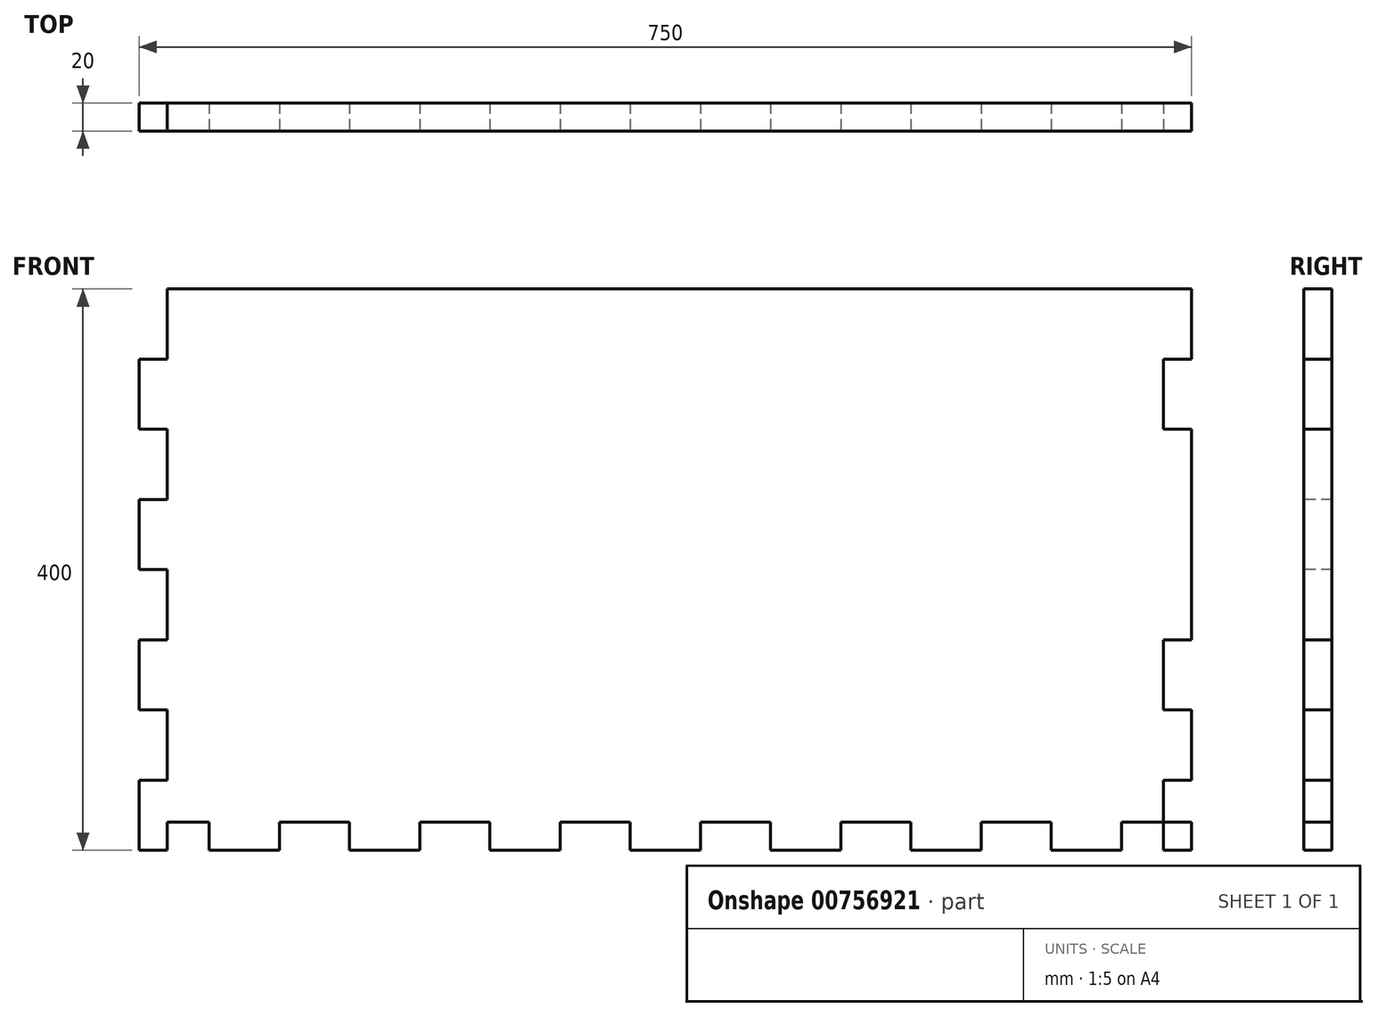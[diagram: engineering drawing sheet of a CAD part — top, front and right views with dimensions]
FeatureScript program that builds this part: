
annotation { "Feature Type Name" : "Feature", "Feature Type Description" : "" }
export const myFeature = defineFeature(function(context is Context, id is Id, definition is map)
    precondition{}
    {
        {
            var Q0;
            Q0=qCreatedBy(makeId("Front.planeOp"),FACE);
            var sketch = newSketch(context, id + "F0", { "sketchPlane" : qUnion([Q0])});
            skLineSegment(sketch, "E0.bottom", {"start": v(-370.9, 0) * mm, "end": v(379.1, 0) * mm});
            skLineSegment(sketch, "E0.top", {"start": v(-370.9, -400) * mm, "end": v(379.1, -400) * mm});
            skLineSegment(sketch, "E0.left", {"start": v(-370.9, 0) * mm, "end": v(-370.9, -400) * mm});
            skLineSegment(sketch, "E0.right", {"start": v(379.1, 0) * mm, "end": v(379.1, -400) * mm});
            skSolve(sketch);
        }
        {
            var Q0;
            Q0=makeQuery(id+"F0.imprint","IMPRINT",FACE,{"disambiguationData":[TD([[makeQuery(id+"F0.imprint","IMPRINT",EDGE,{"derivedFrom":sQuery(id+"F0.wireOp",EDGE,"E0.bottom")}),-1.0]])]});
            extrude(context, id + "F1", {"entities" : qUnion([Q0]), "depth" : 20 * mm, "offsetDistance" : 25.4 * mm});
        }
        {
            var Q0;
            Q0=makeQuery(id+"F1.opExtrude","CAP_FACE",FACE,{"disambiguationData":[OSD([sQuery(id+"F0.wireOp",EDGE,"E0.bottom"),sQuery(id+"F0.wireOp",EDGE,"E0.top"),sQuery(id+"F0.wireOp",EDGE,"E0.left"),sQuery(id+"F0.wireOp",EDGE,"E0.right")])],"isStart":false});
            var sketch = newSketch(context, id + "F2", { "sketchPlane" : qUnion([Q0])});
            skLineSegment(sketch, "E1.bottom", {"start": v(-370.9, 0) * mm, "end": v(-350.9, 0) * mm});
            skLineSegment(sketch, "E1.top", {"start": v(-370.9, -50) * mm, "end": v(-350.9, -50) * mm});
            skLineSegment(sketch, "E1.left", {"start": v(-370.9, 0) * mm, "end": v(-370.9, -50) * mm});
            skLineSegment(sketch, "E1.right", {"start": v(-350.9, 0) * mm, "end": v(-350.9, -50) * mm});
            skLineSegment(sketch, "E2.top", {"start": v(-370.9, -100) * mm, "end": v(-350.9, -100) * mm});
            skLineSegment(sketch, "E2.left", {"start": v(-370.9, -50) * mm, "end": v(-370.9, -100) * mm});
            skLineSegment(sketch, "E2.right", {"start": v(-350.9, -50) * mm, "end": v(-350.9, -100) * mm});
            skLineSegment(sketch, "E3.top", {"start": v(-370.9, -150) * mm, "end": v(-350.9, -150) * mm});
            skLineSegment(sketch, "E3.left", {"start": v(-370.9, -100) * mm, "end": v(-370.9, -150) * mm});
            skLineSegment(sketch, "E3.right", {"start": v(-350.9, -100) * mm, "end": v(-350.9, -150) * mm});
            skLineSegment(sketch, "E4.top", {"start": v(-370.9, -200) * mm, "end": v(-350.9, -200) * mm});
            skLineSegment(sketch, "E4.left", {"start": v(-370.9, -150) * mm, "end": v(-370.9, -200) * mm});
            skLineSegment(sketch, "E4.right", {"start": v(-350.9, -150) * mm, "end": v(-350.9, -200) * mm});
            skLineSegment(sketch, "E5.top", {"start": v(-370.9, -250) * mm, "end": v(-350.9, -250) * mm});
            skLineSegment(sketch, "E5.left", {"start": v(-370.9, -200) * mm, "end": v(-370.9, -250) * mm});
            skLineSegment(sketch, "E5.right", {"start": v(-350.9, -200) * mm, "end": v(-350.9, -250) * mm});
            skLineSegment(sketch, "E6.top", {"start": v(-370.9, -300) * mm, "end": v(-350.9, -300) * mm});
            skLineSegment(sketch, "E6.left", {"start": v(-370.9, -250) * mm, "end": v(-370.9, -300) * mm});
            skLineSegment(sketch, "E6.right", {"start": v(-350.9, -250) * mm, "end": v(-350.9, -300) * mm});
            skLineSegment(sketch, "E7.top", {"start": v(-370.9, -350) * mm, "end": v(-350.9, -350) * mm});
            skLineSegment(sketch, "E7.left", {"start": v(-370.9, -300) * mm, "end": v(-370.9, -350) * mm});
            skLineSegment(sketch, "E7.right", {"start": v(-350.9, -300) * mm, "end": v(-350.9, -350) * mm});
            skLineSegment(sketch, "E8.top", {"start": v(-370.9, -400) * mm, "end": v(-350.9, -400) * mm});
            skLineSegment(sketch, "E8.left", {"start": v(-370.9, -350) * mm, "end": v(-370.9, -400) * mm});
            skLineSegment(sketch, "E8.right", {"start": v(-350.9, -350) * mm, "end": v(-350.9, -400) * mm});
            skLineSegment(sketch, "E9.bottom", {"start": v(379.1, 0) * mm, "end": v(359.1, 0) * mm});
            skLineSegment(sketch, "E9.top", {"start": v(379.1, -50) * mm, "end": v(359.1, -50) * mm});
            skLineSegment(sketch, "E9.left", {"start": v(379.1, 0) * mm, "end": v(379.1, -50) * mm});
            skLineSegment(sketch, "E9.right", {"start": v(359.1, 0) * mm, "end": v(359.1, -50) * mm});
            skLineSegment(sketch, "E10.top", {"start": v(379.1, -100) * mm, "end": v(359.1, -100) * mm});
            skLineSegment(sketch, "E10.left", {"start": v(379.1, -50) * mm, "end": v(379.1, -100) * mm});
            skLineSegment(sketch, "E10.right", {"start": v(359.1, -50) * mm, "end": v(359.1, -100) * mm});
            skLineSegment(sketch, "E11.top", {"start": v(379.1, -150) * mm, "end": v(359.1, -150) * mm});
            skLineSegment(sketch, "E11.left", {"start": v(379.1, -100) * mm, "end": v(379.1, -150) * mm});
            skLineSegment(sketch, "E11.right", {"start": v(359.1, -100) * mm, "end": v(359.1, -150) * mm});
            skLineSegment(sketch, "E12.bottom", {"start": v(359.1, -150) * mm, "end": v(379.1, -150) * mm});
            skLineSegment(sketch, "E12.top", {"start": v(359.1, -200) * mm, "end": v(379.1, -200) * mm});
            skLineSegment(sketch, "E12.left", {"start": v(359.1, -150) * mm, "end": v(359.1, -200) * mm});
            skLineSegment(sketch, "E12.right", {"start": v(379.1, -150) * mm, "end": v(379.1, -200) * mm});
            skLineSegment(sketch, "E13.top", {"start": v(359.1, -250) * mm, "end": v(379.1, -250) * mm});
            skLineSegment(sketch, "E13.left", {"start": v(359.1, -200) * mm, "end": v(359.1, -250) * mm});
            skLineSegment(sketch, "E13.right", {"start": v(379.1, -200) * mm, "end": v(379.1, -250) * mm});
            skLineSegment(sketch, "E14.top", {"start": v(359.1, -300) * mm, "end": v(379.1, -300) * mm});
            skLineSegment(sketch, "E14.left", {"start": v(359.1, -250) * mm, "end": v(359.1, -300) * mm});
            skLineSegment(sketch, "E14.right", {"start": v(379.1, -250) * mm, "end": v(379.1, -300) * mm});
            skLineSegment(sketch, "E15.top", {"start": v(359.1, -350) * mm, "end": v(379.1, -350) * mm});
            skLineSegment(sketch, "E15.left", {"start": v(359.1, -300) * mm, "end": v(359.1, -350) * mm});
            skLineSegment(sketch, "E15.right", {"start": v(379.1, -300) * mm, "end": v(379.1, -350) * mm});
            skLineSegment(sketch, "E16.top", {"start": v(359.1, -400) * mm, "end": v(379.1, -400) * mm});
            skLineSegment(sketch, "E16.left", {"start": v(359.1, -350) * mm, "end": v(359.1, -400) * mm});
            skLineSegment(sketch, "E16.right", {"start": v(379.1, -350) * mm, "end": v(379.1, -400) * mm});
            skLineSegment(sketch, "E17.bottom", {"start": v(-320.9, -380) * mm, "end": v(-370.9, -380) * mm});
            skLineSegment(sketch, "E17.top", {"start": v(-320.9, -400) * mm, "end": v(-370.9, -400) * mm});
            skLineSegment(sketch, "E17.left", {"start": v(-320.9, -380) * mm, "end": v(-320.9, -400) * mm});
            skLineSegment(sketch, "E17.right", {"start": v(-370.9, -380) * mm, "end": v(-370.9, -400) * mm});
            skLineSegment(sketch, "E18.bottom", {"start": v(-320.9, -380) * mm, "end": v(-270.9, -380) * mm});
            skLineSegment(sketch, "E18.top", {"start": v(-320.9, -400) * mm, "end": v(-270.9, -400) * mm});
            skLineSegment(sketch, "E18.right", {"start": v(-270.9, -380) * mm, "end": v(-270.9, -400) * mm});
            skLineSegment(sketch, "E19.bottom", {"start": v(-270.9, -380) * mm, "end": v(-220.9, -380) * mm});
            skLineSegment(sketch, "E19.top", {"start": v(-270.9, -400) * mm, "end": v(-220.9, -400) * mm});
            skLineSegment(sketch, "E19.right", {"start": v(-220.9, -380) * mm, "end": v(-220.9, -400) * mm});
            skLineSegment(sketch, "E20.bottom", {"start": v(-220.9, -380) * mm, "end": v(-170.9, -380) * mm});
            skLineSegment(sketch, "E20.top", {"start": v(-220.9, -400) * mm, "end": v(-170.9, -400) * mm});
            skLineSegment(sketch, "E20.right", {"start": v(-170.9, -380) * mm, "end": v(-170.9, -400) * mm});
            skLineSegment(sketch, "E21.bottom", {"start": v(-170.9, -380) * mm, "end": v(-120.9, -380) * mm});
            skLineSegment(sketch, "E21.top", {"start": v(-170.9, -400) * mm, "end": v(-120.9, -400) * mm});
            skLineSegment(sketch, "E21.right", {"start": v(-120.9, -380) * mm, "end": v(-120.9, -400) * mm});
            skLineSegment(sketch, "E22.bottom", {"start": v(-120.9, -380) * mm, "end": v(-70.9, -380) * mm});
            skLineSegment(sketch, "E22.top", {"start": v(-120.9, -400) * mm, "end": v(-70.9, -400) * mm});
            skLineSegment(sketch, "E22.right", {"start": v(-70.9, -380) * mm, "end": v(-70.9, -400) * mm});
            skLineSegment(sketch, "E23.bottom", {"start": v(-70.9, -380) * mm, "end": v(-20.9, -380) * mm});
            skLineSegment(sketch, "E23.top", {"start": v(-70.9, -400) * mm, "end": v(-20.9, -400) * mm});
            skLineSegment(sketch, "E23.right", {"start": v(-20.9, -380) * mm, "end": v(-20.9, -400) * mm});
            skLineSegment(sketch, "E24.bottom", {"start": v(-20.9, -380) * mm, "end": v(29.1, -380) * mm});
            skLineSegment(sketch, "E24.top", {"start": v(-20.9, -400) * mm, "end": v(29.1, -400) * mm});
            skLineSegment(sketch, "E24.right", {"start": v(29.1, -380) * mm, "end": v(29.1, -400) * mm});
            skLineSegment(sketch, "E25.bottom", {"start": v(29.1, -380) * mm, "end": v(79.1, -380) * mm});
            skLineSegment(sketch, "E25.top", {"start": v(29.1, -400) * mm, "end": v(79.1, -400) * mm});
            skLineSegment(sketch, "E25.right", {"start": v(79.1, -380) * mm, "end": v(79.1, -400) * mm});
            skLineSegment(sketch, "E26.bottom", {"start": v(79.1, -380) * mm, "end": v(129.1, -380) * mm});
            skLineSegment(sketch, "E26.top", {"start": v(79.1, -400) * mm, "end": v(129.1, -400) * mm});
            skLineSegment(sketch, "E26.right", {"start": v(129.1, -380) * mm, "end": v(129.1, -400) * mm});
            skLineSegment(sketch, "E27.bottom", {"start": v(129.1, -380) * mm, "end": v(179.1, -380) * mm});
            skLineSegment(sketch, "E27.top", {"start": v(129.1, -400) * mm, "end": v(179.1, -400) * mm});
            skLineSegment(sketch, "E27.right", {"start": v(179.1, -380) * mm, "end": v(179.1, -400) * mm});
            skLineSegment(sketch, "E28.bottom", {"start": v(179.1, -380) * mm, "end": v(229.1, -380) * mm});
            skLineSegment(sketch, "E28.top", {"start": v(179.1, -400) * mm, "end": v(229.1, -400) * mm});
            skLineSegment(sketch, "E28.right", {"start": v(229.1, -380) * mm, "end": v(229.1, -400) * mm});
            skLineSegment(sketch, "E29.bottom", {"start": v(229.1, -380) * mm, "end": v(279.1, -380) * mm});
            skLineSegment(sketch, "E29.top", {"start": v(229.1, -400) * mm, "end": v(279.1, -400) * mm});
            skLineSegment(sketch, "E29.right", {"start": v(279.1, -380) * mm, "end": v(279.1, -400) * mm});
            skLineSegment(sketch, "E30.bottom", {"start": v(279.1, -380) * mm, "end": v(329.1, -380) * mm});
            skLineSegment(sketch, "E30.top", {"start": v(279.1, -400) * mm, "end": v(329.1, -400) * mm});
            skLineSegment(sketch, "E30.right", {"start": v(329.1, -380) * mm, "end": v(329.1, -400) * mm});
            skLineSegment(sketch, "E31.bottom", {"start": v(329.1, -380) * mm, "end": v(379.1, -380) * mm});
            skLineSegment(sketch, "E31.top", {"start": v(329.1, -400) * mm, "end": v(379.1, -400) * mm});
            skLineSegment(sketch, "E31.right", {"start": v(379.1, -380) * mm, "end": v(379.1, -400) * mm});
            skSolve(sketch);
        }
        {
            var Q0;
            Q0=makeQuery(id+"F2.imprint","IMPRINT",FACE,{"disambiguationData":[TD([[makeQuery(id+"F2.imprint","IMPRINT",EDGE,{"derivedFrom":sQuery(id+"F2.wireOp",EDGE,"E1.bottom")}),-1.0]])]});
            var Q1;
            Q1=makeQuery(id+"F2.imprint","IMPRINT",FACE,{"disambiguationData":[TD([[makeQuery(id+"F2.imprint","IMPRINT",EDGE,{"derivedFrom":sQuery(id+"F2.wireOp",EDGE,"E2.top")}),-1.0]])]});
            var Q2;
            Q2=makeQuery(id+"F2.imprint","IMPRINT",FACE,{"disambiguationData":[TD([[makeQuery(id+"F2.imprint","IMPRINT",EDGE,{"derivedFrom":sQuery(id+"F2.wireOp",EDGE,"E4.top")}),-1.0]])]});
            var Q3;
            Q3=makeQuery(id+"F2.imprint","IMPRINT",FACE,{"disambiguationData":[TD([[makeQuery(id+"F2.imprint","IMPRINT",EDGE,{"derivedFrom":sQuery(id+"F2.wireOp",EDGE,"E6.top")}),-1.0]])]});
            var Q4;
            Q4=makeQuery(id+"F2.imprint","IMPRINT",FACE,{"disambiguationData":[TD([[makeQuery(id+"F2.imprint","IMPRINT",EDGE,{"derivedFrom":sQuery(id+"F2.wireOp",EDGE,"E15.top")}),-1.0]])]});
            var Q5;
            Q5=makeQuery(id+"F2.imprint","IMPRINT",FACE,{"disambiguationData":[TD([[makeQuery(id+"F2.imprint","IMPRINT",EDGE,{"derivedFrom":sQuery(id+"F2.wireOp",EDGE,"E13.top")}),-1.0]])]});
            var Q6;
            Q6=makeQuery(id+"F2.imprint","IMPRINT",FACE,{"disambiguationData":[TD([[makeQuery(id+"F2.imprint","IMPRINT",EDGE,{"derivedFrom":sQuery(id+"F2.wireOp",EDGE,"E12.bottom")}),-1.0]])]});
            var Q7;
            Q7=makeQuery(id+"F2.imprint","IMPRINT",FACE,{"disambiguationData":[TD([[makeQuery(id+"F2.imprint","IMPRINT",EDGE,{"derivedFrom":sQuery(id+"F2.wireOp",EDGE,"E9.top")}),1.0]])]});
            extrude(context, id + "F3", {"entities" : qUnion([Q0, Q1, Q2, Q3, Q4, Q5, Q6, Q7]), "operationType" : NewBodyOperationType.REMOVE, "oppositeDirection" : true, "depth" : 20 * mm, "offsetDistance" : 25.4 * mm});
        }
        {
            var Q0;
            {var subQ5=sQuery(id+"F2.wireOp",EDGE,"E17.right");Q0=makeQuery(id+"F2.imprint","IMPRINT",FACE,{"disambiguationData":[TD([[makeQuery(id+"F2.imprint","IMPRINT",EDGE,{"derivedFrom":subQ5}),1.0]])]});}
            var Q1;
            {var subQ5=sQuery(id+"F2.wireOp",EDGE,"E17.left");Q1=makeQuery(id+"F2.imprint","IMPRINT",FACE,{"disambiguationData":[TD([[makeQuery(id+"F2.imprint","IMPRINT",EDGE,{"derivedFrom":subQ5}),-1.0]])]});}
            var Q2;
            Q2=makeQuery(id+"F2.imprint","IMPRINT",FACE,{"disambiguationData":[TD([[makeQuery(id+"F2.imprint","IMPRINT",EDGE,{"derivedFrom":sQuery(id+"F2.wireOp",EDGE,"E19.bottom")}),-1.0]])]});
            var Q3;
            Q3=makeQuery(id+"F2.imprint","IMPRINT",FACE,{"disambiguationData":[TD([[makeQuery(id+"F2.imprint","IMPRINT",EDGE,{"derivedFrom":sQuery(id+"F2.wireOp",EDGE,"E21.bottom")}),-1.0]])]});
            var Q4;
            Q4=makeQuery(id+"F2.imprint","IMPRINT",FACE,{"disambiguationData":[TD([[makeQuery(id+"F2.imprint","IMPRINT",EDGE,{"derivedFrom":sQuery(id+"F2.wireOp",EDGE,"E23.bottom")}),-1.0]])]});
            var Q5;
            Q5=makeQuery(id+"F2.imprint","IMPRINT",FACE,{"disambiguationData":[TD([[makeQuery(id+"F2.imprint","IMPRINT",EDGE,{"derivedFrom":sQuery(id+"F2.wireOp",EDGE,"E25.bottom")}),-1.0]])]});
            var Q6;
            Q6=makeQuery(id+"F2.imprint","IMPRINT",FACE,{"disambiguationData":[TD([[makeQuery(id+"F2.imprint","IMPRINT",EDGE,{"derivedFrom":sQuery(id+"F2.wireOp",EDGE,"E27.bottom")}),-1.0]])]});
            var Q7;
            Q7=makeQuery(id+"F2.imprint","IMPRINT",FACE,{"disambiguationData":[TD([[makeQuery(id+"F2.imprint","IMPRINT",EDGE,{"derivedFrom":sQuery(id+"F2.wireOp",EDGE,"E29.bottom")}),-1.0]])]});
            var Q8;
            {var subQ5=sQuery(id+"F2.wireOp",EDGE,"E30.right");Q8=makeQuery(id+"F2.imprint","IMPRINT",FACE,{"disambiguationData":[TD([[makeQuery(id+"F2.imprint","IMPRINT",EDGE,{"derivedFrom":subQ5}),1.0]])]});}
            var Q9;
            {var subQ5=sQuery(id+"F2.wireOp",EDGE,"E31.right");Q9=makeQuery(id+"F2.imprint","IMPRINT",FACE,{"disambiguationData":[TD([[makeQuery(id+"F2.imprint","IMPRINT",EDGE,{"derivedFrom":subQ5}),-1.0]])]});}
            extrude(context, id + "F4", {"entities" : qUnion([Q0, Q1, Q2, Q3, Q4, Q5, Q6, Q7, Q8, Q9]), "operationType" : NewBodyOperationType.REMOVE, "oppositeDirection" : true, "depth" : 20 * mm, "offsetDistance" : 25.4 * mm});
        }
    });
